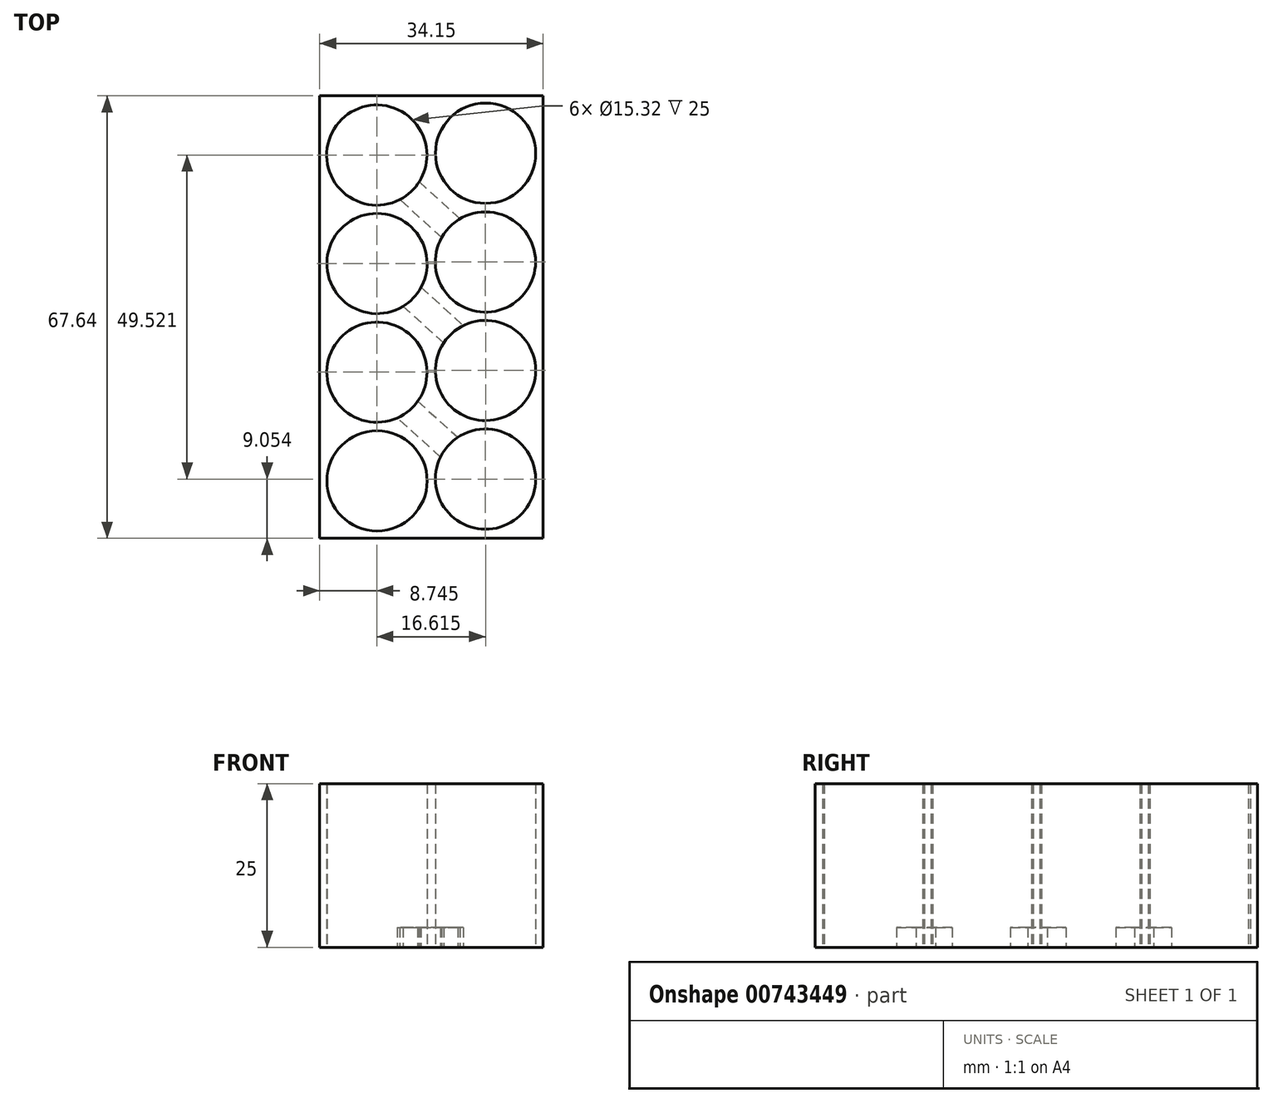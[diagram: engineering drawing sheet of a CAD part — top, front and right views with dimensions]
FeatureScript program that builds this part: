
annotation { "Feature Type Name" : "Feature", "Feature Type Description" : "" }
export const myFeature = defineFeature(function(context is Context, id is Id, definition is map)
    precondition{}
    {
        {
            var Q0;
            Q0=qCreatedBy(makeId("Top.planeOp"),FACE);
            var sketch = newSketch(context, id + "F0", { "sketchPlane" : qUnion([Q0])});
            skCircle(sketch, "E0", {"center": v(9.07, 26.4) * mm, "radius": 7.66 * mm});
            skCircle(sketch, "E1", {"center": v(-7.56, 26.12) * mm, "radius": 7.66 * mm});
            skCircle(sketch, "E2", {"center": v(-7.53, 9.54) * mm, "radius": 7.66 * mm});
            skCircle(sketch, "E3", {"center": v(9.04, 9.77) * mm, "radius": 7.66 * mm});
            skCircle(sketch, "E4", {"center": v(-7.54, -7.06) * mm, "radius": 7.66 * mm});
            skCircle(sketch, "E5", {"center": v(9.06, -6.8) * mm, "radius": 7.66 * mm});
            skCircle(sketch, "E6", {"center": v(9.05, -23.4) * mm, "radius": 7.66 * mm});
            skCircle(sketch, "E7", {"center": v(-7.52, -23.67) * mm, "radius": 7.66 * mm});
            skLineSegment(sketch, "E8.bottom", {"start": v(17.85, 35.18) * mm, "end": v(-16.3, 35.18) * mm, "construction": true});
            skLineSegment(sketch, "E8.top", {"start": v(17.85, -32.46) * mm, "end": v(-16.3, -32.46) * mm, "construction": true});
            skLineSegment(sketch, "E8.left", {"start": v(17.85, 35.18) * mm, "end": v(17.85, -32.46) * mm, "construction": true});
            skLineSegment(sketch, "E8.right", {"start": v(-16.3, 35.18) * mm, "end": v(-16.3, -32.46) * mm, "construction": true});
            skLineSegment(sketch, "E9.bottom", {"start": v(17.85, 35.18) * mm, "end": v(-16.3, 35.18) * mm});
            skLineSegment(sketch, "E9.top", {"start": v(17.85, -32.46) * mm, "end": v(-16.3, -32.46) * mm});
            skLineSegment(sketch, "E9.left", {"start": v(17.85, 35.18) * mm, "end": v(17.85, -32.46) * mm});
            skLineSegment(sketch, "E9.right", {"start": v(-16.3, 35.18) * mm, "end": v(-16.3, -32.46) * mm});
            skLineSegment(sketch, "E10", {"start": v(2.87, 13.04) * mm, "end": v(-4.38, 19.63) * mm});
            skLineSegment(sketch, "E11", {"start": v(-1.7, 22.59) * mm, "end": v(5.56, 16) * mm});
            skLineSegment(sketch, "E12", {"start": v(2.87, 13.04) * mm, "end": v(5.56, 16) * mm});
            skLineSegment(sketch, "E13", {"start": v(-1.7, 22.59) * mm, "end": v(-4.38, 19.63) * mm});
            skLineSegment(sketch, "E14", {"start": v(3.2, -3.1) * mm, "end": v(-4.06, 3.49) * mm});
            skLineSegment(sketch, "E15", {"start": v(-1.37, 6.45) * mm, "end": v(5.88, -0.13) * mm});
            skLineSegment(sketch, "E16", {"start": v(3.2, -3.1) * mm, "end": v(5.88, -0.13) * mm});
            skLineSegment(sketch, "E17", {"start": v(-1.37, 6.45) * mm, "end": v(-4.06, 3.49) * mm});
            skLineSegment(sketch, "E18", {"start": v(2.35, -20.2) * mm, "end": v(-4.9, -13.61) * mm});
            skLineSegment(sketch, "E19", {"start": v(-2.22, -10.65) * mm, "end": v(5.04, -17.24) * mm});
            skLineSegment(sketch, "E20", {"start": v(2.35, -20.2) * mm, "end": v(5.04, -17.24) * mm});
            skLineSegment(sketch, "E21", {"start": v(-2.22, -10.65) * mm, "end": v(-4.9, -13.61) * mm});
            skSolve(sketch);
        }
        {
            var Q0;
            Q0=makeQuery(id+"F0.imprint","IMPRINT",FACE,{"disambiguationData":[TD([[makeQuery(id+"F0.imprint","IMPRINT",EDGE,{"derivedFrom":sQuery(id+"F0.wireOp",EDGE,"E0")}),-1.0]])]});
            var Q1;
            {var subQ0=sQuery(id+"F0.wireOp",EDGE,"E10");var subQ1=sQuery(id+"F0.wireOp",EDGE,"E1");var subQ2=makeQuery(id+"F0.imprint","INTERSECT",VERTEX,{"derivedFrom":[subQ1,subQ0]});Q1=makeQuery(id+"F0.imprint","IMPRINT",FACE,{"disambiguationData":[TD([[makeQuery(id+"F0.imprint","IMPRINT",EDGE,{"disambiguationData":[TD([[subQ2,-1.0]])],"derivedFrom":subQ1}),-1.0]])]});}
            var Q2;
            {var subQ0=sQuery(id+"F0.wireOp",EDGE,"E14");var subQ1=sQuery(id+"F0.wireOp",EDGE,"E2");var subQ2=makeQuery(id+"F0.imprint","INTERSECT",VERTEX,{"derivedFrom":[subQ1,subQ0]});Q2=makeQuery(id+"F0.imprint","IMPRINT",FACE,{"disambiguationData":[TD([[makeQuery(id+"F0.imprint","IMPRINT",EDGE,{"disambiguationData":[TD([[subQ2,-1.0]])],"derivedFrom":subQ1}),-1.0]])]});}
            var Q3;
            {var subQ0=sQuery(id+"F0.wireOp",EDGE,"E18");var subQ1=sQuery(id+"F0.wireOp",EDGE,"E4");var subQ2=makeQuery(id+"F0.imprint","INTERSECT",VERTEX,{"derivedFrom":[subQ1,subQ0]});Q3=makeQuery(id+"F0.imprint","IMPRINT",FACE,{"disambiguationData":[TD([[makeQuery(id+"F0.imprint","IMPRINT",EDGE,{"disambiguationData":[TD([[subQ2,-1.0]])],"derivedFrom":subQ1}),-1.0]])]});}
            extrude(context, id + "F1", {"entities" : qUnion([Q0, Q1, Q2, Q3]), "depth" : 25 * mm, "offsetDistance" : 25 * mm});
        }
        {
            var Q0;
            {var subQ0=sQuery(id+"F0.wireOp",EDGE,"E10");var subQ1=sQuery(id+"F0.wireOp",EDGE,"E1");var subQ2=makeQuery(id+"F0.imprint","INTERSECT",VERTEX,{"derivedFrom":[subQ1,subQ0]});Q0=makeQuery(id+"F0.imprint","IMPRINT",FACE,{"disambiguationData":[TD([[makeQuery(id+"F0.imprint","IMPRINT",EDGE,{"disambiguationData":[TD([[subQ2,-1.0]])],"derivedFrom":subQ1}),-1.0]])]});}
            var Q1;
            {var subQ0=sQuery(id+"F0.wireOp",EDGE,"E18");var subQ1=sQuery(id+"F0.wireOp",EDGE,"E4");var subQ2=makeQuery(id+"F0.imprint","INTERSECT",VERTEX,{"derivedFrom":[subQ1,subQ0]});Q1=makeQuery(id+"F0.imprint","IMPRINT",FACE,{"disambiguationData":[TD([[makeQuery(id+"F0.imprint","IMPRINT",EDGE,{"disambiguationData":[TD([[subQ2,-1.0]])],"derivedFrom":subQ1}),-1.0]])]});}
            var Q2;
            {var subQ0=sQuery(id+"F0.wireOp",EDGE,"E14");var subQ1=sQuery(id+"F0.wireOp",EDGE,"E2");var subQ2=makeQuery(id+"F0.imprint","INTERSECT",VERTEX,{"derivedFrom":[subQ1,subQ0]});Q2=makeQuery(id+"F0.imprint","IMPRINT",FACE,{"disambiguationData":[TD([[makeQuery(id+"F0.imprint","IMPRINT",EDGE,{"disambiguationData":[TD([[subQ2,-1.0]])],"derivedFrom":subQ1}),-1.0]])]});}
            extrude(context, id + "F2", {"entities" : qUnion([Q0, Q1, Q2]), "operationType" : NewBodyOperationType.REMOVE, "depth" : 3 * mm, "offsetDistance" : 25 * mm});
        }
    });
